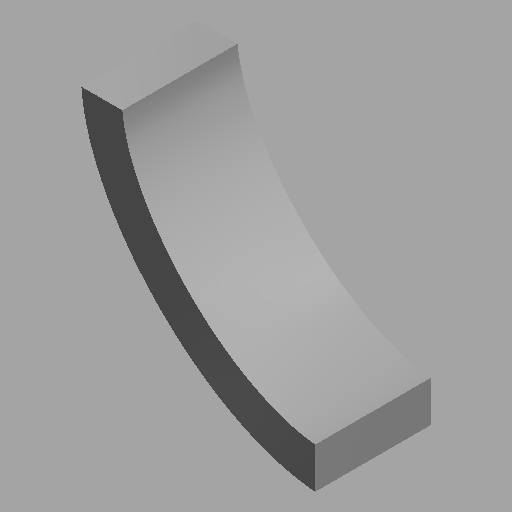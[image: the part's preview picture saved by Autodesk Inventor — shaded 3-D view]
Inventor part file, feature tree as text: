
AUTODESK INVENTOR PART (.ipt)
format: ipt  version: 2023 (Build 270158030, 158C)  size: 114,176 bytes
history: native  units: mm (DEFAULTED — no unit token found)
features: direct_edit x2, other x1, revolve x1, move_body x1
ambient origin geometry x8: Origin, YZ Plane, XZ Plane, XY Plane, X Axis, Y Axis, Z Axis, Center Point
bodies: Solid1 (feature_tree)
feature tree (5):
  other  "Arch header 2 (C)"
  direct_edit  "Direct Edit1"
  direct_edit  "Direct Edit2"
  revolve  "Rotate1"  Angle=135.0deg
  move_body  "Move1"
